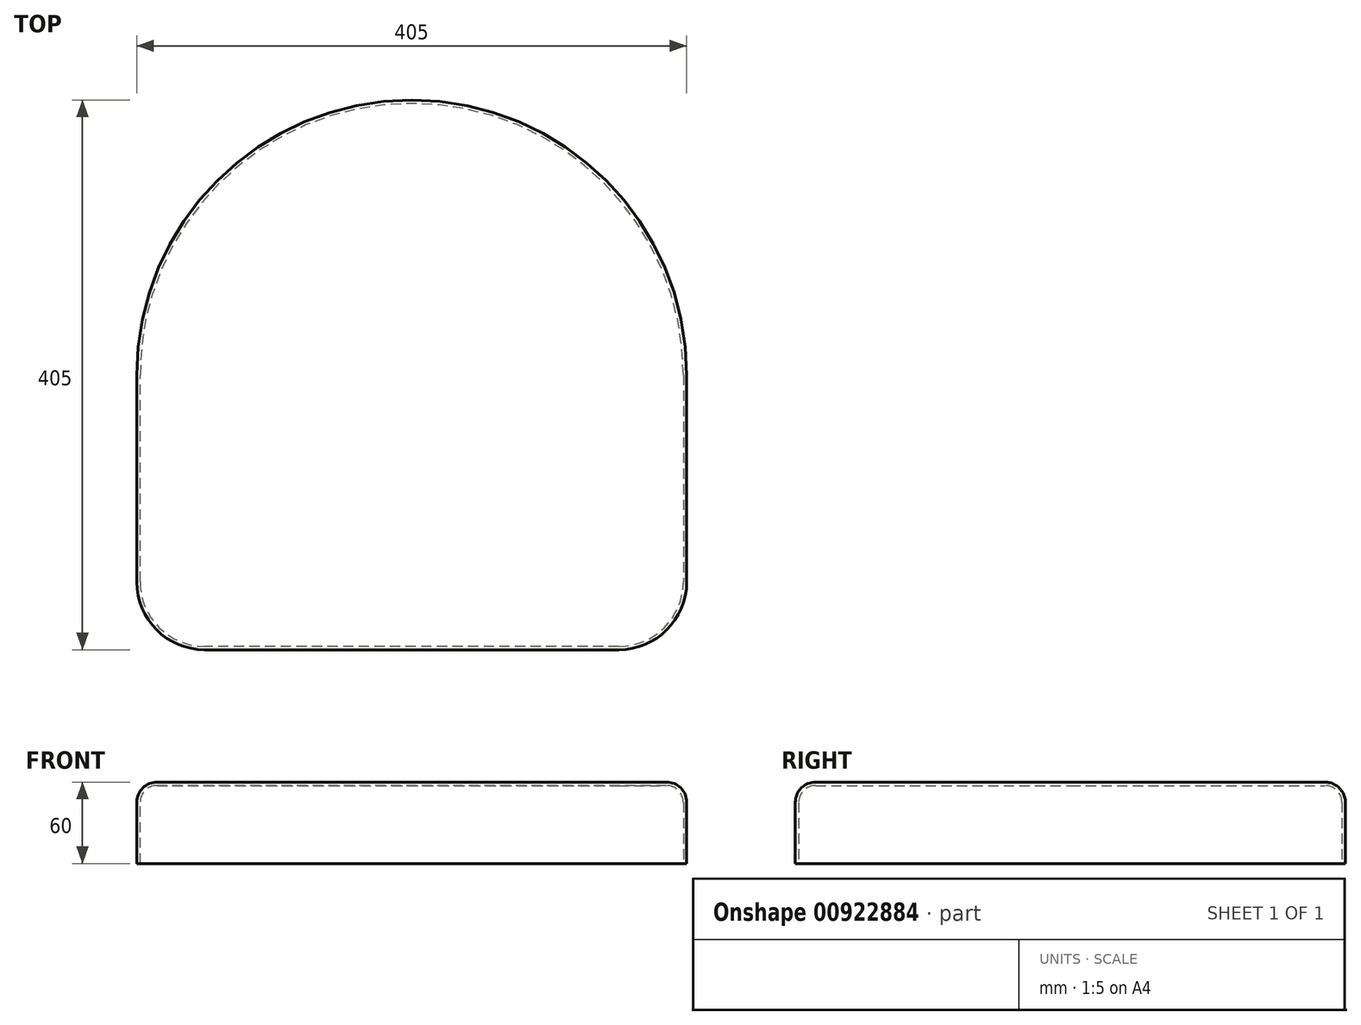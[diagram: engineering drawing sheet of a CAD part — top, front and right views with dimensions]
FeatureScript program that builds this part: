
annotation { "Feature Type Name" : "Feature", "Feature Type Description" : "" }
export const myFeature = defineFeature(function(context is Context, id is Id, definition is map)
    precondition{}
    {
        {
            var Q0;
            Q0=qCreatedBy(makeId("Top.planeOp"),FACE);
            var sketch = newSketch(context, id + "F0", { "sketchPlane" : qUnion([Q0])});
            skArc(sketch, "E0", {"start": v(202.5, 0) * mm, "mid": v(0, 202.5) * mm, "end": v(-202.5, 0) * mm});
            skLineSegment(sketch, "E1", {"start": v(202.5, 0) * mm, "end": v(202.5, -202.5) * mm});
            skLineSegment(sketch, "E2", {"start": v(202.5, -202.5) * mm, "end": v(202.5, -202.5) * mm});
            skLineSegment(sketch, "E3", {"start": v(202.5, -202.5) * mm, "end": v(202.5, 0) * mm});
            skLineSegment(sketch, "E4", {"start": v(202.5, -202.5) * mm, "end": v(-202.5, -202.5) * mm});
            skLineSegment(sketch, "E5", {"start": v(-202.5, -202.5) * mm, "end": v(-202.5, 0) * mm});
            skSolve(sketch);
        }
        {
            var Q0;
            Q0 = qSketchRegion(id + "F0", true);
            extrude(context, id + "F1", {"entities" : qUnion([Q0]), "depth" : 60 * mm, "offsetDistance" : 25 * mm});
        }
        {
            var Q0;
            Q0=makeQuery(id+"F1.opExtrude","SWEPT_EDGE",EDGE,{"disambiguationData":[OSD([sQuery(id+"F0.wireOp",EDGE,"E3"),sQuery(id+"F0.wireOp",EDGE,"E4")])]});
            var Q1;
            Q1=makeQuery(id+"F1.opExtrude","SWEPT_EDGE",EDGE,{"disambiguationData":[OSD([sQuery(id+"F0.wireOp",EDGE,"E4"),sQuery(id+"F0.wireOp",EDGE,"E5")])]});
            fillet(context, id + "F2", {"entities" : qUnion([Q0, Q1]), "radius" : 50 * mm, "tangentPropagation" : true, "allowEdgeOverflow" : false});
        }
        {
            var Q0;
            Q0=makeQuery(id+"F1.opExtrude","CAP_FACE",FACE,{"disambiguationData":[OSD([sQuery(id+"F0.wireOp",EDGE,"E0"),sQuery(id+"F0.wireOp",EDGE,"E3"),sQuery(id+"F0.wireOp",EDGE,"E4"),sQuery(id+"F0.wireOp",EDGE,"E5")])],"isStart":false});
            fillet(context, id + "F3", {"entities" : qUnion([Q0]), "radius" : 15 * mm, "tangentPropagation" : true, "allowEdgeOverflow" : false});
        }
        {
            var Q0;
            Q0=makeQuery(id+"F1.opExtrude","CAP_FACE",FACE,{"disambiguationData":[OSD([sQuery(id+"F0.wireOp",EDGE,"E0"),sQuery(id+"F0.wireOp",EDGE,"E3"),sQuery(id+"F0.wireOp",EDGE,"E4"),sQuery(id+"F0.wireOp",EDGE,"E5")])],"isStart":true});
            shell(context, id + "F4", {"entities" : qUnion([Q0]), "thickness" : 2.5 * mm});
        }
    });
